# Revit family: Hager-VECTOR-Surface_mounted-IP65-With_Cover-With_DIN-NoHosted-PL-pl
name_source: partatom
category: Electrical Equipment
units: mm (PartAtom-declared; Revit-internal decimal feet)

## family parameters
Always vertical = Yes
Cut with Voids When Loaded = No
Maintain Annotation Orientation = No
Panel Configuration = Two Columns, Circuits Across
Part Type = Panelboard
Room Calculation Point = No
Round Connector Dimension = Use Diameter
Shared = No
Work Plane-Based = Yes

## types (30) — shared parameters
Code hager = ADD-EC000214_EU
Default Elevation = 1200 mm
EF000003 - Sposób montażu = Montaż natynkowy
EF000024 - Odporność na promieniowanie UV = No
EF000116 - Numer RAL = 7035
EF000118 - Z płytą montażową = No
EF001062 - Wykonanie zgodne z Dyrektywą Kompatybilności Elektromagnetycznej EMC = No
EF001134 - Szyna DIN = Yes
EF005474 - Stopień ochrony (IP) = IP65
EF006306 - Z zamkiem = No
ETIM class code = EC000214
ETIM class name = Small distribution board
HG000001-Number of columns-pl = 1
HG000002-with door or cover-pl = Yes
HG000003-Range-pl = VECTOR
HG000005-Thickness-pl = 2 mm  [stored 0.00656168 ft]
HG000006-Flush mounted-pl = No
HG000009-Double swing door-pl = No
HG000010-Asymmetric doors-pl = No
HG000011-Empty rows from bottom-pl = No
HG000012-Door swing angle-pl = 90.00°
HG000013-Door on the left-pl = No
HG000014-Door on the right-pl = Yes
HG000015-Clearance visibility-pl = Yes
HG000016-Door 3D visibility-pl = Yes
HG000017-Distance between poles-pl = 18 mm  [stored 0.0590551 ft]
HG000060-RAL-number = 7035
HG000099-Onfly Template ID-pl-PL = 507532
Manufacturer = Hager
Name BIM&CO = Electricity
Name hager = ADD_Enclosures_EC000214
Reference = Template-Enclosure_EU-EC000214
Uniformat = Low Tension Service & Dist.
Uniformat code = D501001
zero-valued in all types: EF000218 - Głębokość wbudowania, EF000332 - Wysokość wbudowania, EF000846 - Szerokość wbudowania, EF001131 - Głębokość wewnętrzna, HG000007-Number of empty columns-pl, HG000008-Number of empty rows-pl

## per-type parameters (varying)
| type | BC_METADATA | EF000007 - Kolor | EF000008 - Szerokość | EF000040 - Wysokość | EF000049 - Głębokość | EF000266 - Liczba rzędów | EF001088 - Możliwość rozbudowy | EF002950 - Szerokość wyrażona liczbą modułów | EF004462 - Rodzaj zamknięcia | EF006244 - Transparentna pokrywa/drzwi | EF009212 - Wykonanie/rodzaj pokrywy | EF015776 - Listwa zaciskowa uziemienia | EF015777 - Listwa zaciskowa przewodu neutralnego | EF015941 - Drzwi przepuszczające sygnał | HG000004-Manufacturer reference-pl | HGEF000266-Liczba rzędów | HGEF0002950-Szerokość wyrażona liczbą modułów |
| VECTOR-Surface_mounted_W111_H175_D93_0_Modular_Spacing-VE103L | {"ObjectGuid":"9abac46e-8686-46ba-9999-39c291c3ddff","ModelGuid":"6dbaf1f9-a988-456c-a727-b82c0d50c8a7","VariantGuid":"448c85be-3390-4f4f-93ef-957195e58bf2","Revision":"#11","VariantName":"VECTOR-Surface_mounted_W111_H175_D93_0_Modular_Spacing-VE103L"} |  | 111 mm | 175 mm  [stored 0.574147 ft] | 93 mm  [stored 0.305118 ft] | 1 | No | 0 |  | No |  | No | No | No | VE103L | 1 | 0 |
| VECTOR-Surface_mounted_W111_H175_D93_3_Modular_Spacing-VE103PN | {"ObjectGuid":"9abac46e-8686-46ba-9999-39c291c3ddff","ModelGuid":"6dbaf1f9-a988-456c-a727-b82c0d50c8a7","VariantGuid":"fbb03e52-8943-4441-bac5-c0a9d37faf79","Revision":"#11","VariantName":"VECTOR-Surface_mounted_W111_H175_D93_3_Modular_Spacing-VE103PN"} | Szary | 111 mm | 175 mm  [stored 0.574147 ft] | 93 mm  [stored 0.305118 ft] | 1 | Yes | 3 | Inne | Yes | Z otworem | No | No | Yes | VE103PN | 1 | 3 |
| VECTOR-Surface_mounted_W111_H175_D93_3_Modular_Spacing-VE103SN | {"ObjectGuid":"9abac46e-8686-46ba-9999-39c291c3ddff","ModelGuid":"6dbaf1f9-a988-456c-a727-b82c0d50c8a7","VariantGuid":"fe525100-8493-4b58-aab5-31db196986d4","Revision":"#11","VariantName":"VECTOR-Surface_mounted_W111_H175_D93_3_Modular_Spacing-VE103SN"} | Szary | 111 mm | 175 mm  [stored 0.574147 ft] | 93 mm  [stored 0.305118 ft] | 1 | Yes | 3 | Inne | Yes | Z otworem | No | No | Yes | VE103SN | 1 | 3 |
| VECTOR-Surface_mounted_W165_H190_D113_0_Modular_Spacing-VE106L | {"ObjectGuid":"9abac46e-8686-46ba-9999-39c291c3ddff","ModelGuid":"6dbaf1f9-a988-456c-a727-b82c0d50c8a7","VariantGuid":"18b4d7eb-23fd-43d4-8ac7-f8a62c8af72e","Revision":"#11","VariantName":"VECTOR-Surface_mounted_W165_H190_D113_0_Modular_Spacing-VE106L"} | Szary | 165 mm | 190 mm  [stored 0.62336 ft] | 113 mm  [stored 0.370735 ft] | 1 | No | 0 | Inne | No | Z otworem | No | No | No | VE106L | 1 | 0 |
| VECTOR-Surface_mounted_W165_H190_D113_6_Modular_Spacing-VE106PN | {"ObjectGuid":"9abac46e-8686-46ba-9999-39c291c3ddff","ModelGuid":"6dbaf1f9-a988-456c-a727-b82c0d50c8a7","VariantGuid":"8ba120be-b3a1-4646-93dd-852b9942699d","Revision":"#11","VariantName":"VECTOR-Surface_mounted_W165_H190_D113_6_Modular_Spacing-VE106PN"} | Szary | 165 mm | 190 mm  [stored 0.62336 ft] | 113 mm  [stored 0.370735 ft] | 1 | Yes | 6 | Inne | Yes | Zamknięty | No | No | Yes | VE106PN | 1 | 6 |
| VECTOR-Surface_mounted_W165_H190_D113_6_Modular_Spacing-VE106SN | {"ObjectGuid":"9abac46e-8686-46ba-9999-39c291c3ddff","ModelGuid":"6dbaf1f9-a988-456c-a727-b82c0d50c8a7","VariantGuid":"949c3a03-fe98-4043-9935-a195efa1684e","Revision":"#11","VariantName":"VECTOR-Surface_mounted_W165_H190_D113_6_Modular_Spacing-VE106SN"} | Szary | 165 mm | 190 mm  [stored 0.62336 ft] | 113 mm  [stored 0.370735 ft] | 1 | Yes | 6 | Inne | Yes | Z otworem | No | No | Yes | VE106SN | 1 | 6 |
| VECTOR-Surface_mounted_W237_H210_D114_10_Modular_Spacing-VE110L | {"ObjectGuid":"9abac46e-8686-46ba-9999-39c291c3ddff","ModelGuid":"6dbaf1f9-a988-456c-a727-b82c0d50c8a7","VariantGuid":"761e4f23-0579-4fbd-b98f-e22ff963acf2","Revision":"#11","VariantName":"VECTOR-Surface_mounted_W237_H210_D114_10_Modular_Spacing-VE110L"} | Szary | 237 mm  [stored 0.777559 ft] | 210 mm  [stored 0.688976 ft] | 114 mm  [stored 0.374016 ft] | 1 | Yes | 10 | Inne | Yes | Z otworem | Yes | Yes | Yes | VE110L | 1 | 10 |
| VECTOR-Surface_mounted_W237_H210_D114_10_Modular_Spacing-VE110PN | {"ObjectGuid":"9abac46e-8686-46ba-9999-39c291c3ddff","ModelGuid":"6dbaf1f9-a988-456c-a727-b82c0d50c8a7","VariantGuid":"6f9dfcf4-705b-42d5-b43a-24a7d90d536d","Revision":"#11","VariantName":"VECTOR-Surface_mounted_W237_H210_D114_10_Modular_Spacing-VE110PN"} | Szary | 237 mm  [stored 0.777559 ft] | 210 mm  [stored 0.688976 ft] | 114 mm  [stored 0.374016 ft] | 1 | Yes | 10 | Inne | Yes | Zamknięty | No | No | Yes | VE110PN | 1 | 10 |
| VECTOR-Surface_mounted_W237_H210_D114_10_Modular_Spacing-VE110SN | {"ObjectGuid":"9abac46e-8686-46ba-9999-39c291c3ddff","ModelGuid":"6dbaf1f9-a988-456c-a727-b82c0d50c8a7","VariantGuid":"419e82ec-403d-4874-9dfa-3dc30382ffe3","Revision":"#11","VariantName":"VECTOR-Surface_mounted_W237_H210_D114_10_Modular_Spacing-VE110SN"} | Szary | 237 mm  [stored 0.777559 ft] | 210 mm  [stored 0.688976 ft] | 114 mm  [stored 0.374016 ft] | 1 | Yes | 10 | Inne | Yes | Zamknięty | No | No | Yes | VE110SN | 1 | 10 |
| VECTOR-Surface_mounted_W310_H302_D151_12_Modular_Spacing-VE112L | {"ObjectGuid":"9abac46e-8686-46ba-9999-39c291c3ddff","ModelGuid":"6dbaf1f9-a988-456c-a727-b82c0d50c8a7","VariantGuid":"51beb4b0-dbc2-44a6-91a8-d6900078eeb5","Revision":"#11","VariantName":"VECTOR-Surface_mounted_W310_H302_D151_12_Modular_Spacing-VE112L"} | Szary | 310 mm  [stored 1.01706 ft] | 302 mm  [stored 0.990814 ft] | 151 mm  [stored 0.495407 ft] | 1 | Yes | 12 | Inne | Yes | Z otworem | Yes | Yes | Yes | VE112L | 1 | 12 |
| VECTOR-Surface_mounted_W310_H302_D151_12_Modular_Spacing-VE112PN | {"ObjectGuid":"9abac46e-8686-46ba-9999-39c291c3ddff","ModelGuid":"6dbaf1f9-a988-456c-a727-b82c0d50c8a7","VariantGuid":"9c53e3c9-61ff-4ca8-a3a5-dd815e4241e2","Revision":"#11","VariantName":"VECTOR-Surface_mounted_W310_H302_D151_12_Modular_Spacing-VE112PN"} | Szary | 310 mm  [stored 1.01706 ft] | 302 mm  [stored 0.990814 ft] | 151 mm  [stored 0.495407 ft] | 1 | Yes | 12 | Inne | Yes | Zamknięty | No | No | Yes | VE112PN | 1 | 12 |
| VECTOR-Surface_mounted_W310_H302_D151_12_Modular_Spacing-VE112SN | {"ObjectGuid":"9abac46e-8686-46ba-9999-39c291c3ddff","ModelGuid":"6dbaf1f9-a988-456c-a727-b82c0d50c8a7","VariantGuid":"e03b5e80-d83a-41a7-af46-b8af0eec4e8a","Revision":"#11","VariantName":"VECTOR-Surface_mounted_W310_H302_D151_12_Modular_Spacing-VE112SN"} | Szary | 310 mm  [stored 1.01706 ft] | 302 mm  [stored 0.990814 ft] | 151 mm  [stored 0.495407 ft] | 1 | Yes | 12 | Inne | Yes | Zamknięty | No | No | Yes | VE112SN | 1 | 12 |
| VECTOR-Surface_mounted_W418_H302_D151_18_Modular_Spacing-VE118L | {"ObjectGuid":"9abac46e-8686-46ba-9999-39c291c3ddff","ModelGuid":"6dbaf1f9-a988-456c-a727-b82c0d50c8a7","VariantGuid":"48f67519-aca6-4eea-a657-8ceeaed2a9be","Revision":"#11","VariantName":"VECTOR-Surface_mounted_W418_H302_D151_18_Modular_Spacing-VE118L"} | Szary | 418 mm  [stored 1.37139 ft] | 302 mm  [stored 0.990814 ft] | 151 mm  [stored 0.495407 ft] | 1 | Yes | 18 | Inne | Yes | Z otworem | Yes | Yes | Yes | VE118L | 1 | 18 |
| VECTOR-Surface_mounted_W418_H302_D151_18_Modular_Spacing-VE118PN | {"ObjectGuid":"9abac46e-8686-46ba-9999-39c291c3ddff","ModelGuid":"6dbaf1f9-a988-456c-a727-b82c0d50c8a7","VariantGuid":"3dabd362-5d2e-4e8b-b9c4-75c55b7b8fdc","Revision":"#11","VariantName":"VECTOR-Surface_mounted_W418_H302_D151_18_Modular_Spacing-VE118PN"} | Szary | 418 mm  [stored 1.37139 ft] | 302 mm  [stored 0.990814 ft] | 151 mm  [stored 0.495407 ft] | 1 | Yes | 18 | Inne | Yes | Zamknięty | No | No | Yes | VE118PN | 1 | 18 |
| VECTOR-Surface_mounted_W418_H302_D151_18_Modular_Spacing-VE118SN | {"ObjectGuid":"9abac46e-8686-46ba-9999-39c291c3ddff","ModelGuid":"6dbaf1f9-a988-456c-a727-b82c0d50c8a7","VariantGuid":"fbd2772f-01b7-430e-a072-0020c1ad3a7a","Revision":"#11","VariantName":"VECTOR-Surface_mounted_W418_H302_D151_18_Modular_Spacing-VE118SN"} | Szary | 418 mm  [stored 1.37139 ft] | 302 mm  [stored 0.990814 ft] | 151 mm  [stored 0.495407 ft] | 1 | Yes | 18 | Inne | Yes | Zamknięty | No | No | Yes | VE118SN | 1 | 18 |
| VECTOR-Surface_mounted_W310_H427_D151_12_Modular_Spacing-VE212L | {"ObjectGuid":"9abac46e-8686-46ba-9999-39c291c3ddff","ModelGuid":"6dbaf1f9-a988-456c-a727-b82c0d50c8a7","VariantGuid":"d4599e4e-7c03-456a-afcf-64f552cbb740","Revision":"#11","VariantName":"VECTOR-Surface_mounted_W310_H427_D151_12_Modular_Spacing-VE212L"} | Szary | 310 mm  [stored 1.01706 ft] | 427 mm  [stored 1.40092 ft] | 151 mm  [stored 0.495407 ft] | 2 | Yes | 12 | Inne | Yes | Z otworem | Yes | Yes | Yes | VE212L | 2 | 12 |
| VECTOR-Surface_mounted_W310_H427_D151_12_Modular_Spacing-VE212PN | {"ObjectGuid":"9abac46e-8686-46ba-9999-39c291c3ddff","ModelGuid":"6dbaf1f9-a988-456c-a727-b82c0d50c8a7","VariantGuid":"d717a2ce-a05c-4e73-9eaf-fabdc6484b30","Revision":"#11","VariantName":"VECTOR-Surface_mounted_W310_H427_D151_12_Modular_Spacing-VE212PN"} | Szary | 310 mm  [stored 1.01706 ft] | 427 mm  [stored 1.40092 ft] | 151 mm  [stored 0.495407 ft] | 2 | Yes | 12 | Inne | Yes | Zamknięty | No | No | Yes | VE212PN | 2 | 12 |
| VECTOR-Surface_mounted_W310_H427_D151_12_Modular_Spacing-VE212SN | {"ObjectGuid":"9abac46e-8686-46ba-9999-39c291c3ddff","ModelGuid":"6dbaf1f9-a988-456c-a727-b82c0d50c8a7","VariantGuid":"b8d19a25-770f-41da-900b-32c23bf11916","Revision":"#11","VariantName":"VECTOR-Surface_mounted_W310_H427_D151_12_Modular_Spacing-VE212SN"} | Szary | 310 mm  [stored 1.01706 ft] | 427 mm  [stored 1.40092 ft] | 151 mm  [stored 0.495407 ft] | 2 | Yes | 12 | Inne | Yes | Zamknięty | No | No | Yes | VE212SN | 2 | 12 |
| VECTOR-Surface_mounted_W418_H452_D151_18_Modular_Spacing-VE218L | {"ObjectGuid":"9abac46e-8686-46ba-9999-39c291c3ddff","ModelGuid":"6dbaf1f9-a988-456c-a727-b82c0d50c8a7","VariantGuid":"4c5426e9-d167-49fe-a873-cf1a0a6da184","Revision":"#11","VariantName":"VECTOR-Surface_mounted_W418_H452_D151_18_Modular_Spacing-VE218L"} | Szary | 418 mm  [stored 1.37139 ft] | 452 mm  [stored 1.48294 ft] | 151 mm  [stored 0.495407 ft] | 2 | Yes | 18 | Inne | Yes | Z otworem | Yes | Yes | Yes | VE218L | 2 | 18 |
| VECTOR-Surface_mounted_W418_H452_D151_18_Modular_Spacing-VE218PN | {"ObjectGuid":"9abac46e-8686-46ba-9999-39c291c3ddff","ModelGuid":"6dbaf1f9-a988-456c-a727-b82c0d50c8a7","VariantGuid":"0a99d492-fcab-4db9-ae9a-ab397207fd8c","Revision":"#11","VariantName":"VECTOR-Surface_mounted_W418_H452_D151_18_Modular_Spacing-VE218PN"} | Szary | 418 mm  [stored 1.37139 ft] | 452 mm  [stored 1.48294 ft] | 151 mm  [stored 0.495407 ft] | 2 | Yes | 18 | Inne | Yes | Zamknięty | No | No | Yes | VE218PN | 2 | 18 |
| VECTOR-Surface_mounted_W418_H452_D151_18_Modular_Spacing-VE218SN | {"ObjectGuid":"9abac46e-8686-46ba-9999-39c291c3ddff","ModelGuid":"6dbaf1f9-a988-456c-a727-b82c0d50c8a7","VariantGuid":"7a42a8c3-3165-4e73-97cf-bd38f30f5900","Revision":"#11","VariantName":"VECTOR-Surface_mounted_W418_H452_D151_18_Modular_Spacing-VE218SN"} | Szary | 418 mm  [stored 1.37139 ft] | 452 mm  [stored 1.48294 ft] | 151 mm  [stored 0.495407 ft] | 2 | Yes | 18 | Inne | Yes | Z otworem | No | No | Yes | VE218SN | 2 | 18 |
| VECTOR-Surface_mounted_W310_H552_D151_12_Modular_Spacing-VE312L | {"ObjectGuid":"9abac46e-8686-46ba-9999-39c291c3ddff","ModelGuid":"6dbaf1f9-a988-456c-a727-b82c0d50c8a7","VariantGuid":"3d6f9d17-b5a8-49d8-9f62-f4822e9bf11f","Revision":"#11","VariantName":"VECTOR-Surface_mounted_W310_H552_D151_12_Modular_Spacing-VE312L"} | Szary | 310 mm  [stored 1.01706 ft] | 552 mm  [stored 1.81102 ft] | 151 mm  [stored 0.495407 ft] | 3 | Yes | 12 | Inne | Yes | Z otworem | Yes | Yes | Yes | VE312L | 3 | 12 |
| VECTOR-Surface_mounted_W310_H552_D151_12_Modular_Spacing-VE312PN | {"ObjectGuid":"9abac46e-8686-46ba-9999-39c291c3ddff","ModelGuid":"6dbaf1f9-a988-456c-a727-b82c0d50c8a7","VariantGuid":"0352363e-4c52-4974-a2bb-1963d041c727","Revision":"#11","VariantName":"VECTOR-Surface_mounted_W310_H552_D151_12_Modular_Spacing-VE312PN"} | Szary | 310 mm  [stored 1.01706 ft] | 552 mm  [stored 1.81102 ft] | 151 mm  [stored 0.495407 ft] | 3 | Yes | 12 | Inne | Yes | Zamknięty | No | No | Yes | VE312PN | 3 | 12 |
| VECTOR-Surface_mounted_W310_H552_D151_12_Modular_Spacing-VE312SN | {"ObjectGuid":"9abac46e-8686-46ba-9999-39c291c3ddff","ModelGuid":"6dbaf1f9-a988-456c-a727-b82c0d50c8a7","VariantGuid":"a154e130-5d5f-4f9d-ba91-e9953c9e79ea","Revision":"#11","VariantName":"VECTOR-Surface_mounted_W310_H552_D151_12_Modular_Spacing-VE312SN"} | Szary | 310 mm  [stored 1.01706 ft] | 552 mm  [stored 1.81102 ft] | 151 mm  [stored 0.495407 ft] | 3 | Yes | 12 | Inne | Yes | Z otworem | No | No | Yes | VE312SN | 3 | 12 |
| VECTOR-Surface_mounted_W418_H602_D151_18_Modular_Spacing-VE318L | {"ObjectGuid":"9abac46e-8686-46ba-9999-39c291c3ddff","ModelGuid":"6dbaf1f9-a988-456c-a727-b82c0d50c8a7","VariantGuid":"ed1110ba-5c90-48d9-8102-8628e7147df5","Revision":"#11","VariantName":"VECTOR-Surface_mounted_W418_H602_D151_18_Modular_Spacing-VE318L"} | Szary | 418 mm  [stored 1.37139 ft] | 602 mm  [stored 1.97507 ft] | 151 mm  [stored 0.495407 ft] | 3 | Yes | 18 | Inne | Yes | Z otworem | Yes | Yes | Yes | VE318L | 3 | 18 |
| VECTOR-Surface_mounted_W418_H602_D151_18_Modular_Spacing-VE318PN | {"ObjectGuid":"9abac46e-8686-46ba-9999-39c291c3ddff","ModelGuid":"6dbaf1f9-a988-456c-a727-b82c0d50c8a7","VariantGuid":"42b6f763-5049-42d6-aa4d-1cb76d30a38e","Revision":"#11","VariantName":"VECTOR-Surface_mounted_W418_H602_D151_18_Modular_Spacing-VE318PN"} | Szary | 418 mm  [stored 1.37139 ft] | 602 mm  [stored 1.97507 ft] | 151 mm  [stored 0.495407 ft] | 3 | Yes | 18 | Inne | Yes | Zamknięty | No | No | Yes | VE318PN | 3 | 18 |
| VECTOR-Surface_mounted_W418_H602_D151_18_Modular_Spacing-VE318SN | {"ObjectGuid":"9abac46e-8686-46ba-9999-39c291c3ddff","ModelGuid":"6dbaf1f9-a988-456c-a727-b82c0d50c8a7","VariantGuid":"a51bab5e-ac4c-4eaf-866d-d5226e1ef8ad","Revision":"#11","VariantName":"VECTOR-Surface_mounted_W418_H602_D151_18_Modular_Spacing-VE318SN"} | Szary | 418 mm  [stored 1.37139 ft] | 602 mm  [stored 1.97507 ft] | 151 mm  [stored 0.495407 ft] | 3 | Yes | 18 | Inne | Yes | Z otworem | No | No | Yes | VE318SN | 3 | 18 |
| VECTOR-Surface_mounted_W310_H677_D151_12_Modular_Spacing-VE412L | {"ObjectGuid":"9abac46e-8686-46ba-9999-39c291c3ddff","ModelGuid":"6dbaf1f9-a988-456c-a727-b82c0d50c8a7","VariantGuid":"2562e534-69e9-434a-8fe5-d085d38d1737","Revision":"#11","VariantName":"VECTOR-Surface_mounted_W310_H677_D151_12_Modular_Spacing-VE412L"} | Szary | 310 mm  [stored 1.01706 ft] | 677 mm  [stored 2.22113 ft] | 151 mm  [stored 0.495407 ft] | 4 | Yes | 12 | Inne | Yes | Z otworem | Yes | Yes | Yes | VE412L | 4 | 12 |
| VECTOR-Surface_mounted_W310_H677_D151_12_Modular_Spacing-VE412PN | {"ObjectGuid":"9abac46e-8686-46ba-9999-39c291c3ddff","ModelGuid":"6dbaf1f9-a988-456c-a727-b82c0d50c8a7","VariantGuid":"814fedca-daf4-4d4f-b17a-ce11ebb56e59","Revision":"#11","VariantName":"VECTOR-Surface_mounted_W310_H677_D151_12_Modular_Spacing-VE412PN"} | Szary | 310 mm  [stored 1.01706 ft] | 677 mm  [stored 2.22113 ft] | 151 mm  [stored 0.495407 ft] | 4 | Yes | 12 | Inne | Yes | Zamknięty | No | No | Yes | VE412PN | 4 | 12 |
| VECTOR-Surface_mounted_W310_H677_D151_12_Modular_Spacing-VE412SN | {"ObjectGuid":"9abac46e-8686-46ba-9999-39c291c3ddff","ModelGuid":"6dbaf1f9-a988-456c-a727-b82c0d50c8a7","VariantGuid":"b71a18c4-2261-432b-be51-31687597c42a","Revision":"#11","VariantName":"VECTOR-Surface_mounted_W310_H677_D151_12_Modular_Spacing-VE412SN"} | Szary | 310 mm  [stored 1.01706 ft] | 677 mm  [stored 2.22113 ft] | 151 mm  [stored 0.495407 ft] | 4 | Yes | 12 | Inne | Yes | Z otworem | No | No | Yes | VE412SN | 4 | 12 |

note: [stored X ft] marks values corroborated as IEEE doubles in the binary element streams (Revit-internal decimal feet)

## geometry (parser evidence)
native form markers: Sweep x16
no freeform markers — native parametric forms only
